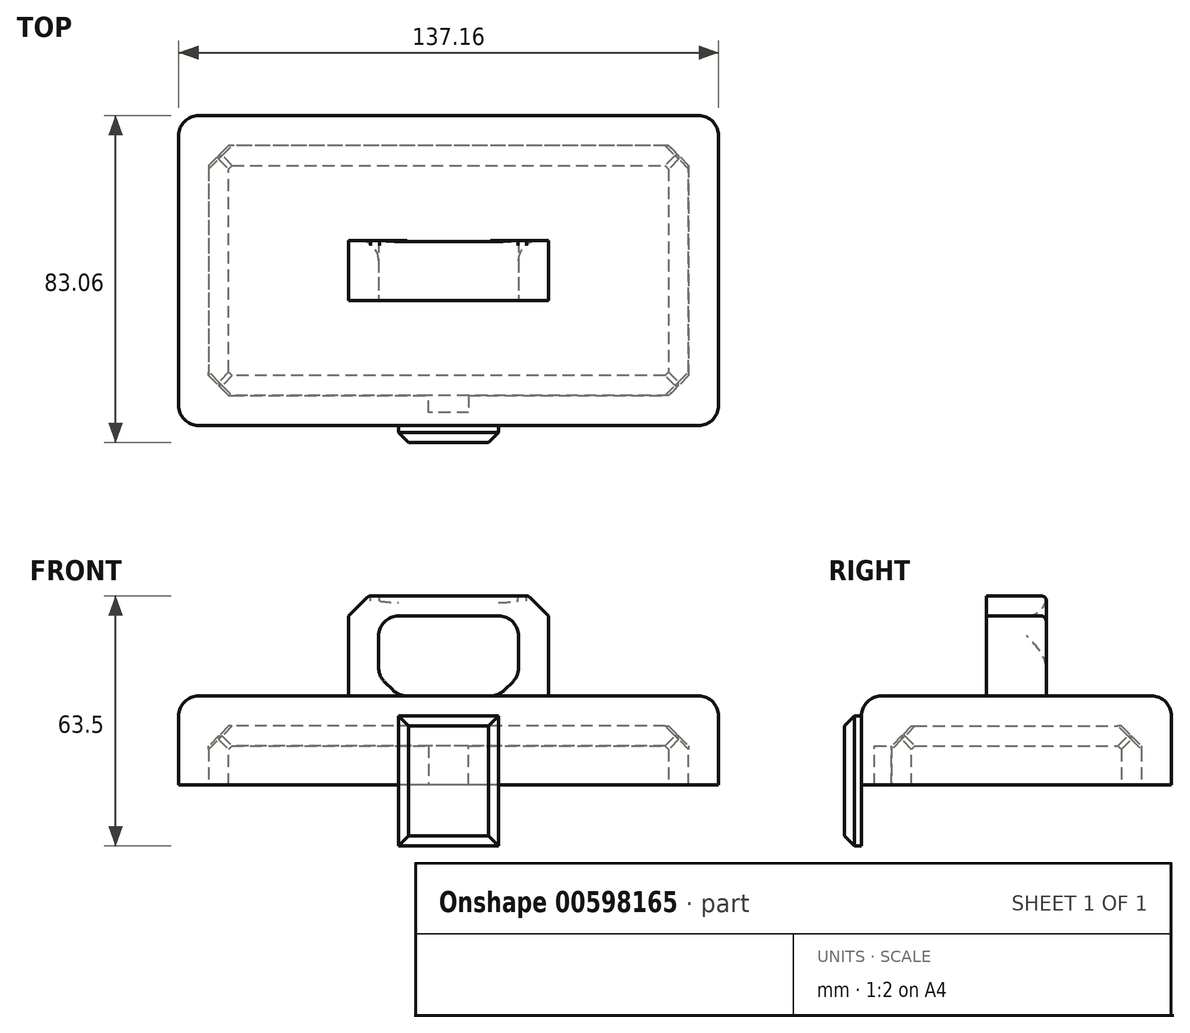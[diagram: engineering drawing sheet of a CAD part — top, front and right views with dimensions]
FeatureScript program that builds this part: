
annotation { "Feature Type Name" : "Feature", "Feature Type Description" : "" }
export const myFeature = defineFeature(function(context is Context, id is Id, definition is map)
    precondition{}
    {
        {
            var Q0;
            Q0=qCreatedBy(makeId("Top.planeOp"),FACE);
            var sketch = newSketch(context, id + "F0", { "sketchPlane" : qUnion([Q0])});
            skLineSegment(sketch, "E0.bottom", {"start": v(68.58, 39.37) * mm, "end": v(-68.58, 39.37) * mm});
            skLineSegment(sketch, "E0.top", {"start": v(68.58, -39.37) * mm, "end": v(-68.58, -39.37) * mm});
            skLineSegment(sketch, "E0.left", {"start": v(68.58, 39.37) * mm, "end": v(68.58, -39.37) * mm});
            skLineSegment(sketch, "E0.right", {"start": v(-68.58, 39.37) * mm, "end": v(-68.58, -39.37) * mm});
            skPoint(sketch, "E0.middle", {"position": v(0, 0) * mm});
            skSolve(sketch);
        }
        {
            var Q0;
            Q0 = qSketchRegion(id + "F0", true);
            extrude(context, id + "F1", {"entities" : qUnion([Q0]), "depth" : 22.6 * mm, "offsetDistance" : 25.4 * mm});
        }
        {
            var Q0;
            Q0=makeQuery(id+"F1.opExtrude","SWEPT_FACE",FACE,{"disambiguationData":[OSD([sQuery(id+"F0.wireOp",EDGE,"E0.top")])]});
            var sketch = newSketch(context, id + "F2", { "sketchPlane" : qUnion([Q0])});
            skLineSegment(sketch, "E1.bottom", {"start": v(-12.7, 17.53) * mm, "end": v(12.7, 17.53) * mm});
            skLineSegment(sketch, "E1.top", {"start": v(-12.7, -15.5) * mm, "end": v(12.7, -15.5) * mm});
            skLineSegment(sketch, "E1.left", {"start": v(-12.7, 17.53) * mm, "end": v(-12.7, -15.5) * mm});
            skLineSegment(sketch, "E1.right", {"start": v(12.7, 17.53) * mm, "end": v(12.7, -15.5) * mm});
            skSolve(sketch);
        }
        {
            var Q0;
            Q0 = qSketchRegion(id + "F2", true);
            extrude(context, id + "F3", {"entities" : qUnion([Q0]), "operationType" : NewBodyOperationType.ADD, "depth" : 4.32 * mm, "offsetDistance" : 25.4 * mm});
        }
        {
            var Q0;
            Q0=makeQuery(id+"F1.opExtrude","CAP_EDGE",EDGE,{"disambiguationData":[OSD([sQuery(id+"F0.wireOp",EDGE,"E0.right")])],"isStart":false});
            var Q1;
            Q1=makeQuery(id+"F1.opExtrude","CAP_EDGE",EDGE,{"disambiguationData":[OSD([sQuery(id+"F0.wireOp",EDGE,"E0.top")])],"isStart":false});
            var Q2;
            Q2=makeQuery(id+"F1.opExtrude","CAP_EDGE",EDGE,{"disambiguationData":[OSD([sQuery(id+"F0.wireOp",EDGE,"E0.left")])],"isStart":false});
            var Q3;
            Q3=makeQuery(id+"F1.opExtrude","CAP_EDGE",EDGE,{"disambiguationData":[OSD([sQuery(id+"F0.wireOp",EDGE,"E0.bottom")])],"isStart":false});
            var Q4;
            Q4=makeQuery(id+"F1.opExtrude","SWEPT_EDGE",EDGE,{"disambiguationData":[OSD([sQuery(id+"F0.wireOp",EDGE,"E0.top"),sQuery(id+"F0.wireOp",EDGE,"E0.left")])]});
            var Q5;
            Q5=makeQuery(id+"F1.opExtrude","SWEPT_EDGE",EDGE,{"disambiguationData":[OSD([sQuery(id+"F0.wireOp",EDGE,"E0.bottom"),sQuery(id+"F0.wireOp",EDGE,"E0.left")])]});
            var Q6;
            Q6=makeQuery(id+"F1.opExtrude","SWEPT_EDGE",EDGE,{"disambiguationData":[OSD([sQuery(id+"F0.wireOp",EDGE,"E0.top"),sQuery(id+"F0.wireOp",EDGE,"E0.right")])]});
            var Q7;
            Q7=makeQuery(id+"F1.opExtrude","SWEPT_EDGE",EDGE,{"disambiguationData":[OSD([sQuery(id+"F0.wireOp",EDGE,"E0.bottom"),sQuery(id+"F0.wireOp",EDGE,"E0.right")])]});
            fillet(context, id + "F4", {"entities" : qUnion([Q0, Q1, Q2, Q3, Q4, Q5, Q6, Q7]), "radius" : 5.08 * mm, "tangentPropagation" : true, "allowEdgeOverflow" : false});
        }
        {
            var Q0;
            Q0=makeQuery(id+"F3.opExtrude","CAP_EDGE",EDGE,{"disambiguationData":[OSD([sQuery(id+"F2.wireOp",EDGE,"E1.bottom")])],"isStart":false});
            var Q1;
            Q1=makeQuery(id+"F3.opExtrude","CAP_EDGE",EDGE,{"disambiguationData":[OSD([sQuery(id+"F2.wireOp",EDGE,"E1.right")])],"isStart":false});
            var Q2;
            Q2=makeQuery(id+"F3.opExtrude","CAP_EDGE",EDGE,{"disambiguationData":[OSD([sQuery(id+"F2.wireOp",EDGE,"E1.left")])],"isStart":false});
            var Q3;
            Q3=makeQuery(id+"F3.opExtrude","CAP_EDGE",EDGE,{"disambiguationData":[OSD([sQuery(id+"F2.wireOp",EDGE,"E1.top")])],"isStart":false});
            chamfer(context, id + "F5", {"entities" : qUnion([Q0, Q1, Q2, Q3]), "width" : 2.54 * mm, "tangentPropagation" : true});
        }
        {
            var Q0;
            Q0=makeQuery(id+"F1.opExtrude","CAP_FACE",FACE,{"disambiguationData":[OSD([sQuery(id+"F0.wireOp",EDGE,"E0.bottom"),sQuery(id+"F0.wireOp",EDGE,"E0.top"),sQuery(id+"F0.wireOp",EDGE,"E0.left"),sQuery(id+"F0.wireOp",EDGE,"E0.right")])],"isStart":true});
            shell(context, id + "F6", {"entities" : qUnion([Q0]), "thickness" : 7.62 * mm});
        }
        {
            var Q0;
            Q0=makeQuery(id+"F6.opShell","OFFSET_EDGE",EDGE,{"disambiguationData":[OSD([sQuery(id+"F0.wireOp",EDGE,"E0.bottom"),sQuery(id+"F0.wireOp",EDGE,"E0.right")])]});
            var Q1;
            Q1=makeQuery(id+"F6.opShell","OFFSET_EDGE",EDGE,{"disambiguationData":[OSD([sQuery(id+"F0.wireOp",EDGE,"E0.top"),sQuery(id+"F0.wireOp",EDGE,"E0.right")])]});
            var Q2;
            Q2=makeQuery(id+"F6.opShell","OFFSET_EDGE",EDGE,{"disambiguationData":[OSD([sQuery(id+"F0.wireOp",EDGE,"E0.bottom"),sQuery(id+"F0.wireOp",EDGE,"E0.left")])]});
            var Q3;
            Q3=makeQuery(id+"F6.opShell","OFFSET_EDGE",EDGE,{"disambiguationData":[OSD([sQuery(id+"F0.wireOp",EDGE,"E0.top"),sQuery(id+"F0.wireOp",EDGE,"E0.left")])]});
            chamfer(context, id + "F7", {"entities" : qUnion([Q0, Q1, Q2, Q3]), "width" : 5.08 * mm, "tangentPropagation" : true});
        }
        {
            var Q0;
            {var subQ0=sQuery(id+"F0.wireOp",EDGE,"E0.right");var subQ1=sQuery(id+"F0.wireOp",EDGE,"E0.left");var subQ2=sQuery(id+"F0.wireOp",EDGE,"E0.top");var subQ3=sQuery(id+"F0.wireOp",EDGE,"E0.bottom");var subQ4=makeQuery(id+"F1.opExtrude","CAP_EDGE",EDGE,{"disambiguationData":[OSD([subQ3])],"isStart":false});Q0=makeQuery(id+"F6.opShell","OFFSET_EDGE",EDGE,{"disambiguationData":[OSD([subQ3,subQ2,subQ1,subQ0]),TDD([makeQuery(id+"F4.opFillet","BLEND_EDGE",EDGE,{"blendedFrom":[subQ4,makeQuery(id+"F1.opExtrude","SWEPT_FACE",FACE,{"disambiguationData":[OSD([subQ3])]})],"blendedInto":[makeQuery(id+"F1.opExtrude","SWEPT_FACE",FACE,{"disambiguationData":[OSD([subQ3])]})]}),makeQuery(id+"F4.opFillet","BLEND_EDGE",EDGE,{"blendedFrom":[subQ4,makeQuery(id+"F1.opExtrude","CAP_FACE",FACE,{"disambiguationData":[OSD([subQ3,subQ2,subQ1,subQ0])],"isStart":false})],"blendedInto":[makeQuery(id+"F1.opExtrude","CAP_FACE",FACE,{"disambiguationData":[OSD([subQ3,subQ2,subQ1,subQ0])],"isStart":false})]})])]});}
            var Q1;
            {var subQ0=sQuery(id+"F0.wireOp",EDGE,"E0.right");var subQ1=makeQuery(id+"F1.opExtrude","CAP_EDGE",EDGE,{"disambiguationData":[OSD([subQ0])],"isStart":false});var subQ2=sQuery(id+"F0.wireOp",EDGE,"E0.left");var subQ3=sQuery(id+"F0.wireOp",EDGE,"E0.top");var subQ4=sQuery(id+"F0.wireOp",EDGE,"E0.bottom");Q1=makeQuery(id+"F6.opShell","OFFSET_EDGE",EDGE,{"disambiguationData":[OSD([subQ4,subQ3,subQ2,subQ0]),TDD([makeQuery(id+"F4.opFillet","BLEND_EDGE",EDGE,{"blendedFrom":[subQ1,makeQuery(id+"F1.opExtrude","CAP_FACE",FACE,{"disambiguationData":[OSD([subQ4,subQ3,subQ2,subQ0])],"isStart":false})],"blendedInto":[makeQuery(id+"F1.opExtrude","CAP_FACE",FACE,{"disambiguationData":[OSD([subQ4,subQ3,subQ2,subQ0])],"isStart":false})]}),makeQuery(id+"F4.opFillet","BLEND_EDGE",EDGE,{"blendedFrom":[subQ1,makeQuery(id+"F1.opExtrude","SWEPT_FACE",FACE,{"disambiguationData":[OSD([subQ0])]})],"blendedInto":[makeQuery(id+"F1.opExtrude","SWEPT_FACE",FACE,{"disambiguationData":[OSD([subQ0])]})]})])]});}
            var Q2;
            {var subQ0=sQuery(id+"F0.wireOp",EDGE,"E0.left");var subQ1=makeQuery(id+"F1.opExtrude","CAP_EDGE",EDGE,{"disambiguationData":[OSD([subQ0])],"isStart":false});var subQ2=sQuery(id+"F0.wireOp",EDGE,"E0.right");var subQ3=sQuery(id+"F0.wireOp",EDGE,"E0.top");var subQ4=sQuery(id+"F0.wireOp",EDGE,"E0.bottom");Q2=makeQuery(id+"F6.opShell","OFFSET_EDGE",EDGE,{"disambiguationData":[OSD([subQ4,subQ3,subQ0,subQ2]),TDD([makeQuery(id+"F4.opFillet","BLEND_EDGE",EDGE,{"blendedFrom":[subQ1,makeQuery(id+"F1.opExtrude","CAP_FACE",FACE,{"disambiguationData":[OSD([subQ4,subQ3,subQ0,subQ2])],"isStart":false})],"blendedInto":[makeQuery(id+"F1.opExtrude","CAP_FACE",FACE,{"disambiguationData":[OSD([subQ4,subQ3,subQ0,subQ2])],"isStart":false})]}),makeQuery(id+"F4.opFillet","BLEND_EDGE",EDGE,{"blendedFrom":[subQ1,makeQuery(id+"F1.opExtrude","SWEPT_FACE",FACE,{"disambiguationData":[OSD([subQ0])]})],"blendedInto":[makeQuery(id+"F1.opExtrude","SWEPT_FACE",FACE,{"disambiguationData":[OSD([subQ0])]})]})])]});}
            var Q3;
            {var subQ0=sQuery(id+"F0.wireOp",EDGE,"E0.top");var subQ1=makeQuery(id+"F1.opExtrude","SWEPT_FACE",FACE,{"disambiguationData":[OSD([subQ0])]});var subQ2=makeQuery(id+"F1.opExtrude","CAP_EDGE",EDGE,{"disambiguationData":[OSD([subQ0])],"isStart":false});var subQ3=sQuery(id+"F0.wireOp",EDGE,"E0.right");var subQ4=sQuery(id+"F0.wireOp",EDGE,"E0.left");var subQ5=sQuery(id+"F0.wireOp",EDGE,"E0.bottom");Q3=makeQuery(id+"F6.opShell","OFFSET_EDGE",EDGE,{"disambiguationData":[OSD([subQ5,subQ0,subQ4,subQ3]),TDD([makeQuery(id+"F4.opFillet","BLEND_EDGE",EDGE,{"blendedFrom":[subQ2,makeQuery(id+"F1.opExtrude","CAP_FACE",FACE,{"disambiguationData":[OSD([subQ5,subQ0,subQ4,subQ3])],"isStart":false})],"blendedInto":[makeQuery(id+"F1.opExtrude","CAP_FACE",FACE,{"disambiguationData":[OSD([subQ5,subQ0,subQ4,subQ3])],"isStart":false})]}),makeQuery(id+"F4.opFillet","BLEND_EDGE",EDGE,{"disambiguationData":[OD(0.0)],"blendedFrom":[subQ2,subQ1],"blendedInto":[subQ1]}),makeQuery(id+"F4.opFillet","BLEND_EDGE",EDGE,{"disambiguationData":[OD(1.0)],"blendedFrom":[subQ2,subQ1],"blendedInto":[subQ1]})])]});}
            chamfer(context, id + "F8", {"entities" : qUnion([Q0, Q1, Q2, Q3]), "width" : 5.08 * mm, "tangentPropagation" : true});
        }
        {
            var Q0;
            {var subQ0=sQuery(id+"F0.wireOp",EDGE,"E0.left");var subQ1=makeQuery(id+"F1.opExtrude","CAP_EDGE",EDGE,{"disambiguationData":[OSD([subQ0])],"isStart":false});var subQ2=sQuery(id+"F0.wireOp",EDGE,"E0.right");var subQ3=sQuery(id+"F0.wireOp",EDGE,"E0.top");var subQ4=sQuery(id+"F0.wireOp",EDGE,"E0.bottom");var subQ5=makeQuery(id+"F1.opExtrude","CAP_FACE",FACE,{"disambiguationData":[OSD([subQ4,subQ3,subQ0,subQ2])],"isStart":false});var subQ6=makeQuery(id+"F1.opExtrude","CAP_EDGE",EDGE,{"disambiguationData":[OSD([subQ4])],"isStart":false});Q0=makeQuery(id+"F8.opChamfer","BLEND_EDGE",EDGE,{"blendedFrom":[makeQuery(id+"F6.opShell","OFFSET_EDGE",EDGE,{"disambiguationData":[OSD([subQ4,subQ3,subQ0,subQ2]),TDD([makeQuery(id+"F4.opFillet","BLEND_EDGE",EDGE,{"blendedFrom":[subQ6,makeQuery(id+"F1.opExtrude","SWEPT_FACE",FACE,{"disambiguationData":[OSD([subQ4])]})],"blendedInto":[makeQuery(id+"F1.opExtrude","SWEPT_FACE",FACE,{"disambiguationData":[OSD([subQ4])]})]}),makeQuery(id+"F4.opFillet","BLEND_EDGE",EDGE,{"blendedFrom":[subQ6,subQ5],"blendedInto":[subQ5]})])]}),makeQuery(id+"F6.opShell","OFFSET_EDGE",EDGE,{"disambiguationData":[OSD([subQ4,subQ3,subQ0,subQ2]),TDD([makeQuery(id+"F4.opFillet","BLEND_EDGE",EDGE,{"blendedFrom":[subQ1,subQ5],"blendedInto":[subQ5]}),makeQuery(id+"F4.opFillet","BLEND_EDGE",EDGE,{"blendedFrom":[subQ1,makeQuery(id+"F1.opExtrude","SWEPT_FACE",FACE,{"disambiguationData":[OSD([subQ0])]})],"blendedInto":[makeQuery(id+"F1.opExtrude","SWEPT_FACE",FACE,{"disambiguationData":[OSD([subQ0])]})]})])]})],"blendedInto":[]});}
            var Q1;
            {var subQ0=sQuery(id+"F0.wireOp",EDGE,"E0.left");var subQ1=sQuery(id+"F0.wireOp",EDGE,"E0.bottom");var subQ2=sQuery(id+"F0.wireOp",EDGE,"E0.right");var subQ3=sQuery(id+"F0.wireOp",EDGE,"E0.top");var subQ4=makeQuery(id+"F1.opExtrude","CAP_EDGE",EDGE,{"disambiguationData":[OSD([subQ1])],"isStart":false});Q1=makeQuery(id+"F8.opChamfer","BLEND_EDGE",EDGE,{"blendedFrom":[makeQuery(id+"F6.opShell","OFFSET_EDGE",EDGE,{"disambiguationData":[OSD([subQ1,subQ3,subQ0,subQ2]),TDD([makeQuery(id+"F4.opFillet","BLEND_EDGE",EDGE,{"blendedFrom":[subQ4,makeQuery(id+"F1.opExtrude","SWEPT_FACE",FACE,{"disambiguationData":[OSD([subQ1])]})],"blendedInto":[makeQuery(id+"F1.opExtrude","SWEPT_FACE",FACE,{"disambiguationData":[OSD([subQ1])]})]}),makeQuery(id+"F4.opFillet","BLEND_EDGE",EDGE,{"blendedFrom":[subQ4,makeQuery(id+"F1.opExtrude","CAP_FACE",FACE,{"disambiguationData":[OSD([subQ1,subQ3,subQ0,subQ2])],"isStart":false})],"blendedInto":[makeQuery(id+"F1.opExtrude","CAP_FACE",FACE,{"disambiguationData":[OSD([subQ1,subQ3,subQ0,subQ2])],"isStart":false})]})])]}),makeQuery(id+"F7.opChamfer","BLEND_FACE",FACE,{"disambiguationData":[OSD([subQ1,subQ0])]})],"blendedInto":[makeQuery(id+"F7.opChamfer","BLEND_FACE",FACE,{"disambiguationData":[OSD([subQ1,subQ0])]})]});}
            var Q2;
            {var subQ0=sQuery(id+"F0.wireOp",EDGE,"E0.left");var subQ1=sQuery(id+"F0.wireOp",EDGE,"E0.bottom");var subQ2=makeQuery(id+"F1.opExtrude","CAP_EDGE",EDGE,{"disambiguationData":[OSD([subQ0])],"isStart":false});var subQ3=sQuery(id+"F0.wireOp",EDGE,"E0.right");var subQ4=sQuery(id+"F0.wireOp",EDGE,"E0.top");Q2=makeQuery(id+"F8.opChamfer","BLEND_EDGE",EDGE,{"blendedFrom":[makeQuery(id+"F6.opShell","OFFSET_EDGE",EDGE,{"disambiguationData":[OSD([subQ1,subQ4,subQ0,subQ3]),TDD([makeQuery(id+"F4.opFillet","BLEND_EDGE",EDGE,{"blendedFrom":[subQ2,makeQuery(id+"F1.opExtrude","CAP_FACE",FACE,{"disambiguationData":[OSD([subQ1,subQ4,subQ0,subQ3])],"isStart":false})],"blendedInto":[makeQuery(id+"F1.opExtrude","CAP_FACE",FACE,{"disambiguationData":[OSD([subQ1,subQ4,subQ0,subQ3])],"isStart":false})]}),makeQuery(id+"F4.opFillet","BLEND_EDGE",EDGE,{"blendedFrom":[subQ2,makeQuery(id+"F1.opExtrude","SWEPT_FACE",FACE,{"disambiguationData":[OSD([subQ0])]})],"blendedInto":[makeQuery(id+"F1.opExtrude","SWEPT_FACE",FACE,{"disambiguationData":[OSD([subQ0])]})]})])]}),makeQuery(id+"F7.opChamfer","BLEND_FACE",FACE,{"disambiguationData":[OSD([subQ1,subQ0])]})],"blendedInto":[makeQuery(id+"F7.opChamfer","BLEND_FACE",FACE,{"disambiguationData":[OSD([subQ1,subQ0])]})]});}
            var Q3;
            {var subQ0=sQuery(id+"F0.wireOp",EDGE,"E0.right");var subQ1=makeQuery(id+"F1.opExtrude","CAP_EDGE",EDGE,{"disambiguationData":[OSD([subQ0])],"isStart":false});var subQ2=sQuery(id+"F0.wireOp",EDGE,"E0.left");var subQ3=sQuery(id+"F0.wireOp",EDGE,"E0.top");var subQ4=sQuery(id+"F0.wireOp",EDGE,"E0.bottom");var subQ5=makeQuery(id+"F1.opExtrude","CAP_FACE",FACE,{"disambiguationData":[OSD([subQ4,subQ3,subQ2,subQ0])],"isStart":false});var subQ6=makeQuery(id+"F1.opExtrude","CAP_EDGE",EDGE,{"disambiguationData":[OSD([subQ4])],"isStart":false});Q3=makeQuery(id+"F8.opChamfer","BLEND_EDGE",EDGE,{"blendedFrom":[makeQuery(id+"F6.opShell","OFFSET_EDGE",EDGE,{"disambiguationData":[OSD([subQ4,subQ3,subQ2,subQ0]),TDD([makeQuery(id+"F4.opFillet","BLEND_EDGE",EDGE,{"blendedFrom":[subQ6,makeQuery(id+"F1.opExtrude","SWEPT_FACE",FACE,{"disambiguationData":[OSD([subQ4])]})],"blendedInto":[makeQuery(id+"F1.opExtrude","SWEPT_FACE",FACE,{"disambiguationData":[OSD([subQ4])]})]}),makeQuery(id+"F4.opFillet","BLEND_EDGE",EDGE,{"blendedFrom":[subQ6,subQ5],"blendedInto":[subQ5]})])]}),makeQuery(id+"F6.opShell","OFFSET_EDGE",EDGE,{"disambiguationData":[OSD([subQ4,subQ3,subQ2,subQ0]),TDD([makeQuery(id+"F4.opFillet","BLEND_EDGE",EDGE,{"blendedFrom":[subQ1,subQ5],"blendedInto":[subQ5]}),makeQuery(id+"F4.opFillet","BLEND_EDGE",EDGE,{"blendedFrom":[subQ1,makeQuery(id+"F1.opExtrude","SWEPT_FACE",FACE,{"disambiguationData":[OSD([subQ0])]})],"blendedInto":[makeQuery(id+"F1.opExtrude","SWEPT_FACE",FACE,{"disambiguationData":[OSD([subQ0])]})]})])]})],"blendedInto":[]});}
            var Q4;
            {var subQ0=sQuery(id+"F0.wireOp",EDGE,"E0.right");var subQ1=sQuery(id+"F0.wireOp",EDGE,"E0.bottom");var subQ2=makeQuery(id+"F1.opExtrude","CAP_EDGE",EDGE,{"disambiguationData":[OSD([subQ0])],"isStart":false});var subQ3=sQuery(id+"F0.wireOp",EDGE,"E0.left");var subQ4=sQuery(id+"F0.wireOp",EDGE,"E0.top");Q4=makeQuery(id+"F8.opChamfer","BLEND_EDGE",EDGE,{"blendedFrom":[makeQuery(id+"F6.opShell","OFFSET_EDGE",EDGE,{"disambiguationData":[OSD([subQ1,subQ4,subQ3,subQ0]),TDD([makeQuery(id+"F4.opFillet","BLEND_EDGE",EDGE,{"blendedFrom":[subQ2,makeQuery(id+"F1.opExtrude","CAP_FACE",FACE,{"disambiguationData":[OSD([subQ1,subQ4,subQ3,subQ0])],"isStart":false})],"blendedInto":[makeQuery(id+"F1.opExtrude","CAP_FACE",FACE,{"disambiguationData":[OSD([subQ1,subQ4,subQ3,subQ0])],"isStart":false})]}),makeQuery(id+"F4.opFillet","BLEND_EDGE",EDGE,{"blendedFrom":[subQ2,makeQuery(id+"F1.opExtrude","SWEPT_FACE",FACE,{"disambiguationData":[OSD([subQ0])]})],"blendedInto":[makeQuery(id+"F1.opExtrude","SWEPT_FACE",FACE,{"disambiguationData":[OSD([subQ0])]})]})])]}),makeQuery(id+"F7.opChamfer","BLEND_FACE",FACE,{"disambiguationData":[OSD([subQ1,subQ0])]})],"blendedInto":[makeQuery(id+"F7.opChamfer","BLEND_FACE",FACE,{"disambiguationData":[OSD([subQ1,subQ0])]})]});}
            var Q5;
            {var subQ0=sQuery(id+"F0.wireOp",EDGE,"E0.right");var subQ1=sQuery(id+"F0.wireOp",EDGE,"E0.bottom");var subQ2=sQuery(id+"F0.wireOp",EDGE,"E0.left");var subQ3=sQuery(id+"F0.wireOp",EDGE,"E0.top");var subQ4=makeQuery(id+"F1.opExtrude","CAP_EDGE",EDGE,{"disambiguationData":[OSD([subQ1])],"isStart":false});Q5=makeQuery(id+"F8.opChamfer","BLEND_EDGE",EDGE,{"blendedFrom":[makeQuery(id+"F6.opShell","OFFSET_EDGE",EDGE,{"disambiguationData":[OSD([subQ1,subQ3,subQ2,subQ0]),TDD([makeQuery(id+"F4.opFillet","BLEND_EDGE",EDGE,{"blendedFrom":[subQ4,makeQuery(id+"F1.opExtrude","SWEPT_FACE",FACE,{"disambiguationData":[OSD([subQ1])]})],"blendedInto":[makeQuery(id+"F1.opExtrude","SWEPT_FACE",FACE,{"disambiguationData":[OSD([subQ1])]})]}),makeQuery(id+"F4.opFillet","BLEND_EDGE",EDGE,{"blendedFrom":[subQ4,makeQuery(id+"F1.opExtrude","CAP_FACE",FACE,{"disambiguationData":[OSD([subQ1,subQ3,subQ2,subQ0])],"isStart":false})],"blendedInto":[makeQuery(id+"F1.opExtrude","CAP_FACE",FACE,{"disambiguationData":[OSD([subQ1,subQ3,subQ2,subQ0])],"isStart":false})]})])]}),makeQuery(id+"F7.opChamfer","BLEND_FACE",FACE,{"disambiguationData":[OSD([subQ1,subQ0])]})],"blendedInto":[makeQuery(id+"F7.opChamfer","BLEND_FACE",FACE,{"disambiguationData":[OSD([subQ1,subQ0])]})]});}
            var Q6;
            {var subQ0=sQuery(id+"F0.wireOp",EDGE,"E0.right");var subQ1=makeQuery(id+"F1.opExtrude","CAP_EDGE",EDGE,{"disambiguationData":[OSD([subQ0])],"isStart":false});var subQ2=sQuery(id+"F0.wireOp",EDGE,"E0.left");var subQ3=sQuery(id+"F0.wireOp",EDGE,"E0.top");var subQ4=sQuery(id+"F0.wireOp",EDGE,"E0.bottom");var subQ5=makeQuery(id+"F1.opExtrude","CAP_FACE",FACE,{"disambiguationData":[OSD([subQ4,subQ3,subQ2,subQ0])],"isStart":false});var subQ6=makeQuery(id+"F1.opExtrude","SWEPT_FACE",FACE,{"disambiguationData":[OSD([subQ3])]});var subQ7=makeQuery(id+"F1.opExtrude","CAP_EDGE",EDGE,{"disambiguationData":[OSD([subQ3])],"isStart":false});Q6=makeQuery(id+"F8.opChamfer","BLEND_EDGE",EDGE,{"blendedFrom":[makeQuery(id+"F6.opShell","OFFSET_EDGE",EDGE,{"disambiguationData":[OSD([subQ4,subQ3,subQ2,subQ0]),TDD([makeQuery(id+"F4.opFillet","BLEND_EDGE",EDGE,{"blendedFrom":[subQ7,subQ5],"blendedInto":[subQ5]}),makeQuery(id+"F4.opFillet","BLEND_EDGE",EDGE,{"disambiguationData":[OD(0.0)],"blendedFrom":[subQ7,subQ6],"blendedInto":[subQ6]}),makeQuery(id+"F4.opFillet","BLEND_EDGE",EDGE,{"disambiguationData":[OD(1.0)],"blendedFrom":[subQ7,subQ6],"blendedInto":[subQ6]})])]}),makeQuery(id+"F6.opShell","OFFSET_EDGE",EDGE,{"disambiguationData":[OSD([subQ4,subQ3,subQ2,subQ0]),TDD([makeQuery(id+"F4.opFillet","BLEND_EDGE",EDGE,{"blendedFrom":[subQ1,subQ5],"blendedInto":[subQ5]}),makeQuery(id+"F4.opFillet","BLEND_EDGE",EDGE,{"blendedFrom":[subQ1,makeQuery(id+"F1.opExtrude","SWEPT_FACE",FACE,{"disambiguationData":[OSD([subQ0])]})],"blendedInto":[makeQuery(id+"F1.opExtrude","SWEPT_FACE",FACE,{"disambiguationData":[OSD([subQ0])]})]})])]})],"blendedInto":[]});}
            var Q7;
            {var subQ0=sQuery(id+"F0.wireOp",EDGE,"E0.right");var subQ1=sQuery(id+"F0.wireOp",EDGE,"E0.top");var subQ2=makeQuery(id+"F1.opExtrude","SWEPT_FACE",FACE,{"disambiguationData":[OSD([subQ1])]});var subQ3=makeQuery(id+"F1.opExtrude","CAP_EDGE",EDGE,{"disambiguationData":[OSD([subQ1])],"isStart":false});var subQ4=sQuery(id+"F0.wireOp",EDGE,"E0.left");var subQ5=sQuery(id+"F0.wireOp",EDGE,"E0.bottom");Q7=makeQuery(id+"F8.opChamfer","BLEND_EDGE",EDGE,{"blendedFrom":[makeQuery(id+"F6.opShell","OFFSET_EDGE",EDGE,{"disambiguationData":[OSD([subQ5,subQ1,subQ4,subQ0]),TDD([makeQuery(id+"F4.opFillet","BLEND_EDGE",EDGE,{"blendedFrom":[subQ3,makeQuery(id+"F1.opExtrude","CAP_FACE",FACE,{"disambiguationData":[OSD([subQ5,subQ1,subQ4,subQ0])],"isStart":false})],"blendedInto":[makeQuery(id+"F1.opExtrude","CAP_FACE",FACE,{"disambiguationData":[OSD([subQ5,subQ1,subQ4,subQ0])],"isStart":false})]}),makeQuery(id+"F4.opFillet","BLEND_EDGE",EDGE,{"disambiguationData":[OD(0.0)],"blendedFrom":[subQ3,subQ2],"blendedInto":[subQ2]}),makeQuery(id+"F4.opFillet","BLEND_EDGE",EDGE,{"disambiguationData":[OD(1.0)],"blendedFrom":[subQ3,subQ2],"blendedInto":[subQ2]})])]}),makeQuery(id+"F7.opChamfer","BLEND_FACE",FACE,{"disambiguationData":[OSD([subQ1,subQ0])]})],"blendedInto":[makeQuery(id+"F7.opChamfer","BLEND_FACE",FACE,{"disambiguationData":[OSD([subQ1,subQ0])]})]});}
            var Q8;
            {var subQ0=sQuery(id+"F0.wireOp",EDGE,"E0.right");var subQ1=sQuery(id+"F0.wireOp",EDGE,"E0.top");var subQ2=makeQuery(id+"F1.opExtrude","CAP_EDGE",EDGE,{"disambiguationData":[OSD([subQ0])],"isStart":false});var subQ3=sQuery(id+"F0.wireOp",EDGE,"E0.left");var subQ4=sQuery(id+"F0.wireOp",EDGE,"E0.bottom");Q8=makeQuery(id+"F8.opChamfer","BLEND_EDGE",EDGE,{"blendedFrom":[makeQuery(id+"F6.opShell","OFFSET_EDGE",EDGE,{"disambiguationData":[OSD([subQ4,subQ1,subQ3,subQ0]),TDD([makeQuery(id+"F4.opFillet","BLEND_EDGE",EDGE,{"blendedFrom":[subQ2,makeQuery(id+"F1.opExtrude","CAP_FACE",FACE,{"disambiguationData":[OSD([subQ4,subQ1,subQ3,subQ0])],"isStart":false})],"blendedInto":[makeQuery(id+"F1.opExtrude","CAP_FACE",FACE,{"disambiguationData":[OSD([subQ4,subQ1,subQ3,subQ0])],"isStart":false})]}),makeQuery(id+"F4.opFillet","BLEND_EDGE",EDGE,{"blendedFrom":[subQ2,makeQuery(id+"F1.opExtrude","SWEPT_FACE",FACE,{"disambiguationData":[OSD([subQ0])]})],"blendedInto":[makeQuery(id+"F1.opExtrude","SWEPT_FACE",FACE,{"disambiguationData":[OSD([subQ0])]})]})])]}),makeQuery(id+"F7.opChamfer","BLEND_FACE",FACE,{"disambiguationData":[OSD([subQ1,subQ0])]})],"blendedInto":[makeQuery(id+"F7.opChamfer","BLEND_FACE",FACE,{"disambiguationData":[OSD([subQ1,subQ0])]})]});}
            var Q9;
            {var subQ0=sQuery(id+"F0.wireOp",EDGE,"E0.left");var subQ1=makeQuery(id+"F1.opExtrude","CAP_EDGE",EDGE,{"disambiguationData":[OSD([subQ0])],"isStart":false});var subQ2=sQuery(id+"F0.wireOp",EDGE,"E0.right");var subQ3=sQuery(id+"F0.wireOp",EDGE,"E0.top");var subQ4=sQuery(id+"F0.wireOp",EDGE,"E0.bottom");var subQ5=makeQuery(id+"F1.opExtrude","CAP_FACE",FACE,{"disambiguationData":[OSD([subQ4,subQ3,subQ0,subQ2])],"isStart":false});var subQ6=makeQuery(id+"F1.opExtrude","SWEPT_FACE",FACE,{"disambiguationData":[OSD([subQ3])]});var subQ7=makeQuery(id+"F1.opExtrude","CAP_EDGE",EDGE,{"disambiguationData":[OSD([subQ3])],"isStart":false});Q9=makeQuery(id+"F8.opChamfer","BLEND_EDGE",EDGE,{"blendedFrom":[makeQuery(id+"F6.opShell","OFFSET_EDGE",EDGE,{"disambiguationData":[OSD([subQ4,subQ3,subQ0,subQ2]),TDD([makeQuery(id+"F4.opFillet","BLEND_EDGE",EDGE,{"blendedFrom":[subQ7,subQ5],"blendedInto":[subQ5]}),makeQuery(id+"F4.opFillet","BLEND_EDGE",EDGE,{"disambiguationData":[OD(0.0)],"blendedFrom":[subQ7,subQ6],"blendedInto":[subQ6]}),makeQuery(id+"F4.opFillet","BLEND_EDGE",EDGE,{"disambiguationData":[OD(1.0)],"blendedFrom":[subQ7,subQ6],"blendedInto":[subQ6]})])]}),makeQuery(id+"F6.opShell","OFFSET_EDGE",EDGE,{"disambiguationData":[OSD([subQ4,subQ3,subQ0,subQ2]),TDD([makeQuery(id+"F4.opFillet","BLEND_EDGE",EDGE,{"blendedFrom":[subQ1,subQ5],"blendedInto":[subQ5]}),makeQuery(id+"F4.opFillet","BLEND_EDGE",EDGE,{"blendedFrom":[subQ1,makeQuery(id+"F1.opExtrude","SWEPT_FACE",FACE,{"disambiguationData":[OSD([subQ0])]})],"blendedInto":[makeQuery(id+"F1.opExtrude","SWEPT_FACE",FACE,{"disambiguationData":[OSD([subQ0])]})]})])]})],"blendedInto":[]});}
            var Q10;
            {var subQ0=sQuery(id+"F0.wireOp",EDGE,"E0.left");var subQ1=sQuery(id+"F0.wireOp",EDGE,"E0.top");var subQ2=makeQuery(id+"F1.opExtrude","CAP_EDGE",EDGE,{"disambiguationData":[OSD([subQ0])],"isStart":false});var subQ3=sQuery(id+"F0.wireOp",EDGE,"E0.right");var subQ4=sQuery(id+"F0.wireOp",EDGE,"E0.bottom");Q10=makeQuery(id+"F8.opChamfer","BLEND_EDGE",EDGE,{"blendedFrom":[makeQuery(id+"F6.opShell","OFFSET_EDGE",EDGE,{"disambiguationData":[OSD([subQ4,subQ1,subQ0,subQ3]),TDD([makeQuery(id+"F4.opFillet","BLEND_EDGE",EDGE,{"blendedFrom":[subQ2,makeQuery(id+"F1.opExtrude","CAP_FACE",FACE,{"disambiguationData":[OSD([subQ4,subQ1,subQ0,subQ3])],"isStart":false})],"blendedInto":[makeQuery(id+"F1.opExtrude","CAP_FACE",FACE,{"disambiguationData":[OSD([subQ4,subQ1,subQ0,subQ3])],"isStart":false})]}),makeQuery(id+"F4.opFillet","BLEND_EDGE",EDGE,{"blendedFrom":[subQ2,makeQuery(id+"F1.opExtrude","SWEPT_FACE",FACE,{"disambiguationData":[OSD([subQ0])]})],"blendedInto":[makeQuery(id+"F1.opExtrude","SWEPT_FACE",FACE,{"disambiguationData":[OSD([subQ0])]})]})])]}),makeQuery(id+"F7.opChamfer","BLEND_FACE",FACE,{"disambiguationData":[OSD([subQ1,subQ0])]})],"blendedInto":[makeQuery(id+"F7.opChamfer","BLEND_FACE",FACE,{"disambiguationData":[OSD([subQ1,subQ0])]})]});}
            var Q11;
            {var subQ0=sQuery(id+"F0.wireOp",EDGE,"E0.left");var subQ1=sQuery(id+"F0.wireOp",EDGE,"E0.top");var subQ2=makeQuery(id+"F1.opExtrude","SWEPT_FACE",FACE,{"disambiguationData":[OSD([subQ1])]});var subQ3=makeQuery(id+"F1.opExtrude","CAP_EDGE",EDGE,{"disambiguationData":[OSD([subQ1])],"isStart":false});var subQ4=sQuery(id+"F0.wireOp",EDGE,"E0.right");var subQ5=sQuery(id+"F0.wireOp",EDGE,"E0.bottom");Q11=makeQuery(id+"F8.opChamfer","BLEND_EDGE",EDGE,{"blendedFrom":[makeQuery(id+"F6.opShell","OFFSET_EDGE",EDGE,{"disambiguationData":[OSD([subQ5,subQ1,subQ0,subQ4]),TDD([makeQuery(id+"F4.opFillet","BLEND_EDGE",EDGE,{"blendedFrom":[subQ3,makeQuery(id+"F1.opExtrude","CAP_FACE",FACE,{"disambiguationData":[OSD([subQ5,subQ1,subQ0,subQ4])],"isStart":false})],"blendedInto":[makeQuery(id+"F1.opExtrude","CAP_FACE",FACE,{"disambiguationData":[OSD([subQ5,subQ1,subQ0,subQ4])],"isStart":false})]}),makeQuery(id+"F4.opFillet","BLEND_EDGE",EDGE,{"disambiguationData":[OD(0.0)],"blendedFrom":[subQ3,subQ2],"blendedInto":[subQ2]}),makeQuery(id+"F4.opFillet","BLEND_EDGE",EDGE,{"disambiguationData":[OD(1.0)],"blendedFrom":[subQ3,subQ2],"blendedInto":[subQ2]})])]}),makeQuery(id+"F7.opChamfer","BLEND_FACE",FACE,{"disambiguationData":[OSD([subQ1,subQ0])]})],"blendedInto":[makeQuery(id+"F7.opChamfer","BLEND_FACE",FACE,{"disambiguationData":[OSD([subQ1,subQ0])]})]});}
            chamfer(context, id + "F9", {"entities" : qUnion([Q0, Q1, Q2, Q3, Q4, Q5, Q6, Q7, Q8, Q9, Q10, Q11]), "width" : 1.27 * mm, "tangentPropagation" : true});
        }
        {
            var Q0;
            Q0=makeQuery(id+"F1.opExtrude","CAP_FACE",FACE,{"disambiguationData":[OSD([sQuery(id+"F0.wireOp",EDGE,"E0.bottom"),sQuery(id+"F0.wireOp",EDGE,"E0.top"),sQuery(id+"F0.wireOp",EDGE,"E0.left"),sQuery(id+"F0.wireOp",EDGE,"E0.right")])],"isStart":false});
            var sketch = newSketch(context, id + "F10", { "sketchPlane" : qUnion([Q0])});
            skLineSegment(sketch, "E2.bottom", {"start": v(25.4, 7.62) * mm, "end": v(-25.4, 7.62) * mm});
            skLineSegment(sketch, "E2.top", {"start": v(25.4, -7.62) * mm, "end": v(-25.4, -7.62) * mm});
            skLineSegment(sketch, "E2.left", {"start": v(25.4, 7.62) * mm, "end": v(25.4, -7.62) * mm});
            skLineSegment(sketch, "E2.right", {"start": v(-25.4, 7.62) * mm, "end": v(-25.4, -7.62) * mm});
            skPoint(sketch, "E2.middle", {"position": v(0, 0) * mm});
            skSolve(sketch);
        }
        {
            var Q0;
            Q0 = qSketchRegion(id + "F10", true);
            extrude(context, id + "F11", {"entities" : qUnion([Q0]), "operationType" : NewBodyOperationType.ADD, "depth" : 25.4 * mm, "offsetDistance" : 25.4 * mm});
        }
        {
            var Q0;
            Q0=makeQuery(id+"F11.opExtrude","SWEPT_FACE",FACE,{"disambiguationData":[OSD([sQuery(id+"F10.wireOp",EDGE,"E2.top")])]});
            var sketch = newSketch(context, id + "F12", { "sketchPlane" : qUnion([Q0])});
            skLineSegment(sketch, "E3.bottom", {"start": v(-17.78, 22.6) * mm, "end": v(17.78, 22.6) * mm});
            skLineSegment(sketch, "E3.top", {"start": v(-17.78, 42.93) * mm, "end": v(17.78, 42.93) * mm});
            skLineSegment(sketch, "E3.left", {"start": v(-17.78, 22.6) * mm, "end": v(-17.78, 42.93) * mm});
            skLineSegment(sketch, "E3.right", {"start": v(17.78, 22.6) * mm, "end": v(17.78, 42.93) * mm});
            skSolve(sketch);
        }
        {
            var Q0;
            Q0 = qSketchRegion(id + "F12", true);
            extrude(context, id + "F13", {"entities" : qUnion([Q0]), "operationType" : NewBodyOperationType.REMOVE, "oppositeDirection" : true, "depth" : 25.4 * mm, "offsetDistance" : 25.4 * mm});
        }
        {
            var Q0;
            Q0=makeQuery(id+"F11.opExtrude","CAP_EDGE",EDGE,{"disambiguationData":[OSD([sQuery(id+"F10.wireOp",EDGE,"E2.right")])],"isStart":false});
            var Q1;
            Q1=makeQuery(id+"F11.opExtrude","CAP_EDGE",EDGE,{"disambiguationData":[OSD([sQuery(id+"F10.wireOp",EDGE,"E2.left")])],"isStart":false});
            var Q2;
            Q2=makeQuery(id+"F11.opExtrude","CAP_EDGE",EDGE,{"disambiguationData":[OSD([sQuery(id+"F10.wireOp",EDGE,"E2.left")])],"isStart":true});
            var Q3;
            {var subQ0=sQuery(id+"F10.wireOp",EDGE,"E2.top");Q3=makeQuery(id+"F13.boolean.opBoolean","SPLIT",EDGE,{"disambiguationData":[TD([makeQuery(id+"F11.opExtrude","SWEPT_FACE",FACE,{"disambiguationData":[OSD([sQuery(id+"F10.wireOp",EDGE,"E2.left")])]})])],"derivedFrom":makeQuery(id+"F11.opExtrude","CAP_EDGE",EDGE,{"disambiguationData":[OSD([subQ0])],"isStart":true})});}
            var Q4;
            Q4=makeQuery(id+"F13.boolean.opBoolean","COPY",EDGE,{"derivedFrom":makeQuery(id+"F13.opExtrude","SWEPT_EDGE",EDGE,{"disambiguationData":[OSD([sQuery(id+"F10.wireOp",EDGE,"E2.top"),sQuery(id+"F12.wireOp",EDGE,"E3.bottom"),sQuery(id+"F12.wireOp",EDGE,"E3.left")])]})});
            var Q5;
            {var subQ0=sQuery(id+"F10.wireOp",EDGE,"E2.top");Q5=makeQuery(id+"F13.boolean.opBoolean","SPLIT",EDGE,{"disambiguationData":[TD([makeQuery(id+"F11.opExtrude","SWEPT_FACE",FACE,{"disambiguationData":[OSD([sQuery(id+"F10.wireOp",EDGE,"E2.right")])]})])],"derivedFrom":makeQuery(id+"F11.opExtrude","CAP_EDGE",EDGE,{"disambiguationData":[OSD([subQ0])],"isStart":true})});}
            var Q6;
            Q6=makeQuery(id+"F11.opExtrude","CAP_EDGE",EDGE,{"disambiguationData":[OSD([sQuery(id+"F10.wireOp",EDGE,"E2.right")])],"isStart":true});
            var Q7;
            {var subQ0=sQuery(id+"F10.wireOp",EDGE,"E2.bottom");Q7=makeQuery(id+"F13.boolean.opBoolean","SPLIT",EDGE,{"disambiguationData":[TD([makeQuery(id+"F11.opExtrude","SWEPT_FACE",FACE,{"disambiguationData":[OSD([sQuery(id+"F10.wireOp",EDGE,"E2.right")])]})])],"derivedFrom":makeQuery(id+"F11.opExtrude","CAP_EDGE",EDGE,{"disambiguationData":[OSD([subQ0])],"isStart":true})});}
            var Q8;
            {var subQ0=sQuery(id+"F10.wireOp",EDGE,"E2.bottom");Q8=makeQuery(id+"F13.boolean.opBoolean","SPLIT",EDGE,{"disambiguationData":[TD([makeQuery(id+"F11.opExtrude","SWEPT_FACE",FACE,{"disambiguationData":[OSD([sQuery(id+"F10.wireOp",EDGE,"E2.left")])]})])],"derivedFrom":makeQuery(id+"F11.opExtrude","CAP_EDGE",EDGE,{"disambiguationData":[OSD([subQ0])],"isStart":true})});}
            var Q9;
            Q9=makeQuery(id+"F13.boolean.opBoolean","COPY",EDGE,{"derivedFrom":makeQuery(id+"F13.opExtrude","SWEPT_EDGE",EDGE,{"disambiguationData":[OSD([sQuery(id+"F10.wireOp",EDGE,"E2.top"),sQuery(id+"F12.wireOp",EDGE,"E3.bottom"),sQuery(id+"F12.wireOp",EDGE,"E3.right")])]})});
            chamfer(context, id + "F14", {"entities" : qUnion([Q0, Q1, Q2, Q3, Q4, Q5, Q6, Q7, Q8, Q9]), "width" : 5.08 * mm, "tangentPropagation" : true});
        }
        {
            var Q0;
            {var subQ0=sQuery(id+"F10.wireOp",EDGE,"E2.left");Q0=makeQuery(id+"F14.opChamfer","BLEND_EDGE",EDGE,{"blendedFrom":[makeQuery(id+"F11.opExtrude","CAP_EDGE",EDGE,{"disambiguationData":[OSD([subQ0])],"isStart":true}),makeQuery(id+"F11.opExtrude","SWEPT_FACE",FACE,{"disambiguationData":[OSD([subQ0])]})],"blendedInto":[makeQuery(id+"F11.opExtrude","SWEPT_FACE",FACE,{"disambiguationData":[OSD([subQ0])]})]});}
            var Q1;
            {var subQ0=sQuery(id+"F10.wireOp",EDGE,"E2.top");var subQ1=makeQuery(id+"F11.opExtrude","SWEPT_FACE",FACE,{"disambiguationData":[OSD([subQ0])]});Q1=makeQuery(id+"F14.opChamfer","BLEND_EDGE",EDGE,{"blendedFrom":[makeQuery(id+"F13.boolean.opBoolean","SPLIT",EDGE,{"disambiguationData":[TD([makeQuery(id+"F11.opExtrude","SWEPT_FACE",FACE,{"disambiguationData":[OSD([sQuery(id+"F10.wireOp",EDGE,"E2.left")])]})])],"derivedFrom":makeQuery(id+"F11.opExtrude","CAP_EDGE",EDGE,{"disambiguationData":[OSD([subQ0])],"isStart":true})}),subQ1],"blendedInto":[subQ1]});}
            var Q2;
            {var subQ0=sQuery(id+"F10.wireOp",EDGE,"E2.bottom");var subQ1=makeQuery(id+"F11.opExtrude","SWEPT_FACE",FACE,{"disambiguationData":[OSD([subQ0])]});Q2=makeQuery(id+"F14.opChamfer","BLEND_EDGE",EDGE,{"blendedFrom":[makeQuery(id+"F13.boolean.opBoolean","SPLIT",EDGE,{"disambiguationData":[TD([makeQuery(id+"F11.opExtrude","SWEPT_FACE",FACE,{"disambiguationData":[OSD([sQuery(id+"F10.wireOp",EDGE,"E2.left")])]})])],"derivedFrom":makeQuery(id+"F11.opExtrude","CAP_EDGE",EDGE,{"disambiguationData":[OSD([subQ0])],"isStart":true})}),subQ1],"blendedInto":[subQ1]});}
            var Q3;
            {var subQ0=sQuery(id+"F12.wireOp",EDGE,"E3.right");Q3=makeQuery(id+"F14.opChamfer","BLEND_EDGE",EDGE,{"blendedFrom":[makeQuery(id+"F13.boolean.opBoolean","COPY",EDGE,{"derivedFrom":makeQuery(id+"F13.opExtrude","SWEPT_EDGE",EDGE,{"disambiguationData":[OSD([sQuery(id+"F10.wireOp",EDGE,"E2.top"),sQuery(id+"F12.wireOp",EDGE,"E3.bottom"),subQ0])]})}),makeQuery(id+"F13.boolean.opBoolean","COPY",FACE,{"derivedFrom":makeQuery(id+"F13.opExtrude","SWEPT_FACE",FACE,{"disambiguationData":[OSD([subQ0])]})})],"blendedInto":[makeQuery(id+"F13.boolean.opBoolean","COPY",FACE,{"derivedFrom":makeQuery(id+"F13.opExtrude","SWEPT_FACE",FACE,{"disambiguationData":[OSD([subQ0])]})})]});}
            var Q4;
            {var subQ0=sQuery(id+"F10.wireOp",EDGE,"E2.bottom");var subQ1=makeQuery(id+"F11.opExtrude","SWEPT_FACE",FACE,{"disambiguationData":[OSD([subQ0])]});Q4=makeQuery(id+"F14.opChamfer","BLEND_EDGE",EDGE,{"blendedFrom":[makeQuery(id+"F13.boolean.opBoolean","SPLIT",EDGE,{"disambiguationData":[TD([makeQuery(id+"F11.opExtrude","SWEPT_FACE",FACE,{"disambiguationData":[OSD([sQuery(id+"F10.wireOp",EDGE,"E2.right")])]})])],"derivedFrom":makeQuery(id+"F11.opExtrude","CAP_EDGE",EDGE,{"disambiguationData":[OSD([subQ0])],"isStart":true})}),subQ1],"blendedInto":[subQ1]});}
            var Q5;
            {var subQ0=sQuery(id+"F10.wireOp",EDGE,"E2.right");Q5=makeQuery(id+"F14.opChamfer","BLEND_EDGE",EDGE,{"blendedFrom":[makeQuery(id+"F11.opExtrude","CAP_EDGE",EDGE,{"disambiguationData":[OSD([subQ0])],"isStart":true}),makeQuery(id+"F11.opExtrude","SWEPT_FACE",FACE,{"disambiguationData":[OSD([subQ0])]})],"blendedInto":[makeQuery(id+"F11.opExtrude","SWEPT_FACE",FACE,{"disambiguationData":[OSD([subQ0])]})]});}
            var Q6;
            {var subQ0=sQuery(id+"F10.wireOp",EDGE,"E2.top");var subQ1=makeQuery(id+"F11.opExtrude","SWEPT_FACE",FACE,{"disambiguationData":[OSD([subQ0])]});Q6=makeQuery(id+"F14.opChamfer","BLEND_EDGE",EDGE,{"blendedFrom":[makeQuery(id+"F13.boolean.opBoolean","SPLIT",EDGE,{"disambiguationData":[TD([makeQuery(id+"F11.opExtrude","SWEPT_FACE",FACE,{"disambiguationData":[OSD([sQuery(id+"F10.wireOp",EDGE,"E2.right")])]})])],"derivedFrom":makeQuery(id+"F11.opExtrude","CAP_EDGE",EDGE,{"disambiguationData":[OSD([subQ0])],"isStart":true})}),subQ1],"blendedInto":[subQ1]});}
            var Q7;
            {var subQ0=sQuery(id+"F12.wireOp",EDGE,"E3.left");Q7=makeQuery(id+"F14.opChamfer","BLEND_EDGE",EDGE,{"blendedFrom":[makeQuery(id+"F13.boolean.opBoolean","COPY",EDGE,{"derivedFrom":makeQuery(id+"F13.opExtrude","SWEPT_EDGE",EDGE,{"disambiguationData":[OSD([sQuery(id+"F10.wireOp",EDGE,"E2.top"),sQuery(id+"F12.wireOp",EDGE,"E3.bottom"),subQ0])]})}),makeQuery(id+"F13.boolean.opBoolean","COPY",FACE,{"derivedFrom":makeQuery(id+"F13.opExtrude","SWEPT_FACE",FACE,{"disambiguationData":[OSD([subQ0])]})})],"blendedInto":[makeQuery(id+"F13.boolean.opBoolean","COPY",FACE,{"derivedFrom":makeQuery(id+"F13.opExtrude","SWEPT_FACE",FACE,{"disambiguationData":[OSD([subQ0])]})})]});}
            fillet(context, id + "F15", {"entities" : qUnion([Q0, Q1, Q2, Q3, Q4, Q5, Q6, Q7]), "radius" : 5.08 * mm, "tangentPropagation" : true, "allowEdgeOverflow" : false});
        }
        {
            var Q0;
            Q0=makeQuery(id+"F14.opChamfer","BLEND_EDGE",EDGE,{"blendedFrom":[makeQuery(id+"F11.opExtrude","CAP_EDGE",EDGE,{"disambiguationData":[OSD([sQuery(id+"F10.wireOp",EDGE,"E2.left")])],"isStart":true}),makeQuery(id+"F13.boolean.opBoolean","MERGE",FACE,{"derivedFrom":[makeQuery(id+"F1.opExtrude","CAP_FACE",FACE,{"disambiguationData":[OSD([sQuery(id+"F0.wireOp",EDGE,"E0.bottom"),sQuery(id+"F0.wireOp",EDGE,"E0.top"),sQuery(id+"F0.wireOp",EDGE,"E0.left"),sQuery(id+"F0.wireOp",EDGE,"E0.right")])],"isStart":false}),makeQuery(id+"F13.opExtrude","SWEPT_FACE",FACE,{"disambiguationData":[OSD([sQuery(id+"F12.wireOp",EDGE,"E3.bottom")])]})]})],"blendedInto":[makeQuery(id+"F13.boolean.opBoolean","MERGE",FACE,{"derivedFrom":[makeQuery(id+"F1.opExtrude","CAP_FACE",FACE,{"disambiguationData":[OSD([sQuery(id+"F0.wireOp",EDGE,"E0.bottom"),sQuery(id+"F0.wireOp",EDGE,"E0.top"),sQuery(id+"F0.wireOp",EDGE,"E0.left"),sQuery(id+"F0.wireOp",EDGE,"E0.right")])],"isStart":false}),makeQuery(id+"F13.opExtrude","SWEPT_FACE",FACE,{"disambiguationData":[OSD([sQuery(id+"F12.wireOp",EDGE,"E3.bottom")])]})]})]});
            var Q1;
            {var subQ0=makeQuery(id+"F13.opExtrude","SWEPT_FACE",FACE,{"disambiguationData":[OSD([sQuery(id+"F12.wireOp",EDGE,"E3.bottom")])]});var subQ1=makeQuery(id+"F1.opExtrude","CAP_FACE",FACE,{"disambiguationData":[OSD([sQuery(id+"F0.wireOp",EDGE,"E0.bottom"),sQuery(id+"F0.wireOp",EDGE,"E0.top"),sQuery(id+"F0.wireOp",EDGE,"E0.left"),sQuery(id+"F0.wireOp",EDGE,"E0.right")])],"isStart":false});var subQ2=sQuery(id+"F10.wireOp",EDGE,"E2.top");Q1=makeQuery(id+"F14.opChamfer","BLEND_EDGE",EDGE,{"blendedFrom":[makeQuery(id+"F13.boolean.opBoolean","SPLIT",EDGE,{"disambiguationData":[TD([makeQuery(id+"F11.opExtrude","SWEPT_FACE",FACE,{"disambiguationData":[OSD([sQuery(id+"F10.wireOp",EDGE,"E2.left")])]})])],"derivedFrom":makeQuery(id+"F11.opExtrude","CAP_EDGE",EDGE,{"disambiguationData":[OSD([subQ2])],"isStart":true})}),makeQuery(id+"F13.boolean.opBoolean","MERGE",FACE,{"derivedFrom":[subQ1,subQ0]})],"blendedInto":[makeQuery(id+"F13.boolean.opBoolean","MERGE",FACE,{"derivedFrom":[subQ1,subQ0]})]});}
            var Q2;
            {var subQ0=makeQuery(id+"F13.opExtrude","SWEPT_FACE",FACE,{"disambiguationData":[OSD([sQuery(id+"F12.wireOp",EDGE,"E3.bottom")])]});var subQ1=makeQuery(id+"F1.opExtrude","CAP_FACE",FACE,{"disambiguationData":[OSD([sQuery(id+"F0.wireOp",EDGE,"E0.bottom"),sQuery(id+"F0.wireOp",EDGE,"E0.top"),sQuery(id+"F0.wireOp",EDGE,"E0.left"),sQuery(id+"F0.wireOp",EDGE,"E0.right")])],"isStart":false});var subQ2=sQuery(id+"F10.wireOp",EDGE,"E2.bottom");Q2=makeQuery(id+"F14.opChamfer","BLEND_EDGE",EDGE,{"blendedFrom":[makeQuery(id+"F13.boolean.opBoolean","SPLIT",EDGE,{"disambiguationData":[TD([makeQuery(id+"F11.opExtrude","SWEPT_FACE",FACE,{"disambiguationData":[OSD([sQuery(id+"F10.wireOp",EDGE,"E2.left")])]})])],"derivedFrom":makeQuery(id+"F11.opExtrude","CAP_EDGE",EDGE,{"disambiguationData":[OSD([subQ2])],"isStart":true})}),makeQuery(id+"F13.boolean.opBoolean","MERGE",FACE,{"derivedFrom":[subQ1,subQ0]})],"blendedInto":[makeQuery(id+"F13.boolean.opBoolean","MERGE",FACE,{"derivedFrom":[subQ1,subQ0]})]});}
            var Q3;
            {var subQ0=sQuery(id+"F12.wireOp",EDGE,"E3.bottom");Q3=makeQuery(id+"F14.opChamfer","BLEND_EDGE",EDGE,{"blendedFrom":[makeQuery(id+"F13.boolean.opBoolean","COPY",EDGE,{"derivedFrom":makeQuery(id+"F13.opExtrude","SWEPT_EDGE",EDGE,{"disambiguationData":[OSD([sQuery(id+"F10.wireOp",EDGE,"E2.top"),subQ0,sQuery(id+"F12.wireOp",EDGE,"E3.right")])]})}),makeQuery(id+"F13.boolean.opBoolean","MERGE",FACE,{"derivedFrom":[makeQuery(id+"F1.opExtrude","CAP_FACE",FACE,{"disambiguationData":[OSD([sQuery(id+"F0.wireOp",EDGE,"E0.bottom"),sQuery(id+"F0.wireOp",EDGE,"E0.top"),sQuery(id+"F0.wireOp",EDGE,"E0.left"),sQuery(id+"F0.wireOp",EDGE,"E0.right")])],"isStart":false}),makeQuery(id+"F13.opExtrude","SWEPT_FACE",FACE,{"disambiguationData":[OSD([subQ0])]})]})],"blendedInto":[makeQuery(id+"F13.boolean.opBoolean","MERGE",FACE,{"derivedFrom":[makeQuery(id+"F1.opExtrude","CAP_FACE",FACE,{"disambiguationData":[OSD([sQuery(id+"F0.wireOp",EDGE,"E0.bottom"),sQuery(id+"F0.wireOp",EDGE,"E0.top"),sQuery(id+"F0.wireOp",EDGE,"E0.left"),sQuery(id+"F0.wireOp",EDGE,"E0.right")])],"isStart":false}),makeQuery(id+"F13.opExtrude","SWEPT_FACE",FACE,{"disambiguationData":[OSD([subQ0])]})]})]});}
            fillet(context, id + "F16", {"entities" : qUnion([Q0, Q1, Q2, Q3]), "radius" : 5.08 * mm, "tangentPropagation" : true, "allowEdgeOverflow" : false});
        }
        {
            var Q0;
            {var subQ0=sQuery(id+"F12.wireOp",EDGE,"E3.bottom");Q0=makeQuery(id+"F14.opChamfer","BLEND_EDGE",EDGE,{"blendedFrom":[makeQuery(id+"F13.boolean.opBoolean","COPY",EDGE,{"derivedFrom":makeQuery(id+"F13.opExtrude","SWEPT_EDGE",EDGE,{"disambiguationData":[OSD([sQuery(id+"F10.wireOp",EDGE,"E2.top"),subQ0,sQuery(id+"F12.wireOp",EDGE,"E3.left")])]})}),makeQuery(id+"F13.boolean.opBoolean","MERGE",FACE,{"derivedFrom":[makeQuery(id+"F1.opExtrude","CAP_FACE",FACE,{"disambiguationData":[OSD([sQuery(id+"F0.wireOp",EDGE,"E0.bottom"),sQuery(id+"F0.wireOp",EDGE,"E0.top"),sQuery(id+"F0.wireOp",EDGE,"E0.left"),sQuery(id+"F0.wireOp",EDGE,"E0.right")])],"isStart":false}),makeQuery(id+"F13.opExtrude","SWEPT_FACE",FACE,{"disambiguationData":[OSD([subQ0])]})]})],"blendedInto":[makeQuery(id+"F13.boolean.opBoolean","MERGE",FACE,{"derivedFrom":[makeQuery(id+"F1.opExtrude","CAP_FACE",FACE,{"disambiguationData":[OSD([sQuery(id+"F0.wireOp",EDGE,"E0.bottom"),sQuery(id+"F0.wireOp",EDGE,"E0.top"),sQuery(id+"F0.wireOp",EDGE,"E0.left"),sQuery(id+"F0.wireOp",EDGE,"E0.right")])],"isStart":false}),makeQuery(id+"F13.opExtrude","SWEPT_FACE",FACE,{"disambiguationData":[OSD([subQ0])]})]})]});}
            var Q1;
            {var subQ0=makeQuery(id+"F13.opExtrude","SWEPT_FACE",FACE,{"disambiguationData":[OSD([sQuery(id+"F12.wireOp",EDGE,"E3.bottom")])]});var subQ1=makeQuery(id+"F1.opExtrude","CAP_FACE",FACE,{"disambiguationData":[OSD([sQuery(id+"F0.wireOp",EDGE,"E0.bottom"),sQuery(id+"F0.wireOp",EDGE,"E0.top"),sQuery(id+"F0.wireOp",EDGE,"E0.left"),sQuery(id+"F0.wireOp",EDGE,"E0.right")])],"isStart":false});var subQ2=sQuery(id+"F10.wireOp",EDGE,"E2.top");Q1=makeQuery(id+"F14.opChamfer","BLEND_EDGE",EDGE,{"blendedFrom":[makeQuery(id+"F13.boolean.opBoolean","SPLIT",EDGE,{"disambiguationData":[TD([makeQuery(id+"F11.opExtrude","SWEPT_FACE",FACE,{"disambiguationData":[OSD([sQuery(id+"F10.wireOp",EDGE,"E2.right")])]})])],"derivedFrom":makeQuery(id+"F11.opExtrude","CAP_EDGE",EDGE,{"disambiguationData":[OSD([subQ2])],"isStart":true})}),makeQuery(id+"F13.boolean.opBoolean","MERGE",FACE,{"derivedFrom":[subQ1,subQ0]})],"blendedInto":[makeQuery(id+"F13.boolean.opBoolean","MERGE",FACE,{"derivedFrom":[subQ1,subQ0]})]});}
            var Q2;
            Q2=makeQuery(id+"F14.opChamfer","BLEND_EDGE",EDGE,{"blendedFrom":[makeQuery(id+"F11.opExtrude","CAP_EDGE",EDGE,{"disambiguationData":[OSD([sQuery(id+"F10.wireOp",EDGE,"E2.right")])],"isStart":true}),makeQuery(id+"F13.boolean.opBoolean","MERGE",FACE,{"derivedFrom":[makeQuery(id+"F1.opExtrude","CAP_FACE",FACE,{"disambiguationData":[OSD([sQuery(id+"F0.wireOp",EDGE,"E0.bottom"),sQuery(id+"F0.wireOp",EDGE,"E0.top"),sQuery(id+"F0.wireOp",EDGE,"E0.left"),sQuery(id+"F0.wireOp",EDGE,"E0.right")])],"isStart":false}),makeQuery(id+"F13.opExtrude","SWEPT_FACE",FACE,{"disambiguationData":[OSD([sQuery(id+"F12.wireOp",EDGE,"E3.bottom")])]})]})],"blendedInto":[makeQuery(id+"F13.boolean.opBoolean","MERGE",FACE,{"derivedFrom":[makeQuery(id+"F1.opExtrude","CAP_FACE",FACE,{"disambiguationData":[OSD([sQuery(id+"F0.wireOp",EDGE,"E0.bottom"),sQuery(id+"F0.wireOp",EDGE,"E0.top"),sQuery(id+"F0.wireOp",EDGE,"E0.left"),sQuery(id+"F0.wireOp",EDGE,"E0.right")])],"isStart":false}),makeQuery(id+"F13.opExtrude","SWEPT_FACE",FACE,{"disambiguationData":[OSD([sQuery(id+"F12.wireOp",EDGE,"E3.bottom")])]})]})]});
            var Q3;
            {var subQ0=makeQuery(id+"F13.opExtrude","SWEPT_FACE",FACE,{"disambiguationData":[OSD([sQuery(id+"F12.wireOp",EDGE,"E3.bottom")])]});var subQ1=makeQuery(id+"F1.opExtrude","CAP_FACE",FACE,{"disambiguationData":[OSD([sQuery(id+"F0.wireOp",EDGE,"E0.bottom"),sQuery(id+"F0.wireOp",EDGE,"E0.top"),sQuery(id+"F0.wireOp",EDGE,"E0.left"),sQuery(id+"F0.wireOp",EDGE,"E0.right")])],"isStart":false});var subQ2=sQuery(id+"F10.wireOp",EDGE,"E2.bottom");Q3=makeQuery(id+"F14.opChamfer","BLEND_EDGE",EDGE,{"blendedFrom":[makeQuery(id+"F13.boolean.opBoolean","SPLIT",EDGE,{"disambiguationData":[TD([makeQuery(id+"F11.opExtrude","SWEPT_FACE",FACE,{"disambiguationData":[OSD([sQuery(id+"F10.wireOp",EDGE,"E2.right")])]})])],"derivedFrom":makeQuery(id+"F11.opExtrude","CAP_EDGE",EDGE,{"disambiguationData":[OSD([subQ2])],"isStart":true})}),makeQuery(id+"F13.boolean.opBoolean","MERGE",FACE,{"derivedFrom":[subQ1,subQ0]})],"blendedInto":[makeQuery(id+"F13.boolean.opBoolean","MERGE",FACE,{"derivedFrom":[subQ1,subQ0]})]});}
            fillet(context, id + "F17", {"entities" : qUnion([Q0, Q1, Q2, Q3]), "radius" : 5.08 * mm, "tangentPropagation" : true, "allowEdgeOverflow" : false});
        }
        {
            var Q0;
            Q0=makeQuery(id+"F13.boolean.opBoolean","COPY",EDGE,{"derivedFrom":makeQuery(id+"F13.opExtrude","SWEPT_EDGE",EDGE,{"disambiguationData":[OSD([sQuery(id+"F12.wireOp",EDGE,"E3.top"),sQuery(id+"F12.wireOp",EDGE,"E3.right")])]})});
            var Q1;
            Q1=makeQuery(id+"F13.boolean.opBoolean","COPY",EDGE,{"derivedFrom":makeQuery(id+"F13.opExtrude","SWEPT_EDGE",EDGE,{"disambiguationData":[OSD([sQuery(id+"F12.wireOp",EDGE,"E3.top"),sQuery(id+"F12.wireOp",EDGE,"E3.left")])]})});
            var Q2;
            Q2=makeQuery(id+"F13.boolean.opBoolean","COPY",EDGE,{"derivedFrom":makeQuery(id+"F13.opExtrude","CAP_EDGE",EDGE,{"disambiguationData":[OSD([sQuery(id+"F12.wireOp",EDGE,"E3.top")])],"isStart":true})});
            var Q3;
            Q3=makeQuery(id+"F13.boolean.opBoolean","INTERSECT",EDGE,{"derivedFrom":[makeQuery(id+"F11.opExtrude","SWEPT_FACE",FACE,{"disambiguationData":[OSD([sQuery(id+"F10.wireOp",EDGE,"E2.bottom")])]}),makeQuery(id+"F13.opExtrude","SWEPT_FACE",FACE,{"disambiguationData":[OSD([sQuery(id+"F12.wireOp",EDGE,"E3.top")])]})]});
            fillet(context, id + "F18", {"entities" : qUnion([Q0, Q1, Q2, Q3]), "radius" : 5.08 * mm, "tangentPropagation" : true, "allowEdgeOverflow" : false});
        }
        {
            var Q0;
            {var subQ0=sQuery(id+"F10.wireOp",EDGE,"E2.bottom");Q0=makeQuery(id+"F18.opFillet","BLEND_EDGE",EDGE,{"blendedFrom":[makeQuery(id+"F13.boolean.opBoolean","INTERSECT",EDGE,{"derivedFrom":[makeQuery(id+"F11.opExtrude","SWEPT_FACE",FACE,{"disambiguationData":[OSD([subQ0])]}),makeQuery(id+"F13.opExtrude","SWEPT_FACE",FACE,{"disambiguationData":[OSD([sQuery(id+"F12.wireOp",EDGE,"E3.top")])]})]}),makeQuery(id+"F11.opExtrude","CAP_FACE",FACE,{"disambiguationData":[OSD([subQ0,sQuery(id+"F10.wireOp",EDGE,"E2.top"),sQuery(id+"F10.wireOp",EDGE,"E2.left"),sQuery(id+"F10.wireOp",EDGE,"E2.right")])],"isStart":false})],"blendedInto":[makeQuery(id+"F11.opExtrude","CAP_FACE",FACE,{"disambiguationData":[OSD([subQ0,sQuery(id+"F10.wireOp",EDGE,"E2.top"),sQuery(id+"F10.wireOp",EDGE,"E2.left"),sQuery(id+"F10.wireOp",EDGE,"E2.right")])],"isStart":false})]});}
            var Q1;
            Q1=makeQuery(id+"F18.opFillet","BLEND_EDGE",EDGE,{"blendedFrom":[makeQuery(id+"F13.boolean.opBoolean","COPY",EDGE,{"derivedFrom":makeQuery(id+"F13.opExtrude","CAP_EDGE",EDGE,{"disambiguationData":[OSD([sQuery(id+"F12.wireOp",EDGE,"E3.top")])],"isStart":true})}),makeQuery(id+"F11.opExtrude","CAP_FACE",FACE,{"disambiguationData":[OSD([sQuery(id+"F10.wireOp",EDGE,"E2.bottom"),sQuery(id+"F10.wireOp",EDGE,"E2.top"),sQuery(id+"F10.wireOp",EDGE,"E2.left"),sQuery(id+"F10.wireOp",EDGE,"E2.right")])],"isStart":false})],"blendedInto":[makeQuery(id+"F11.opExtrude","CAP_FACE",FACE,{"disambiguationData":[OSD([sQuery(id+"F10.wireOp",EDGE,"E2.bottom"),sQuery(id+"F10.wireOp",EDGE,"E2.top"),sQuery(id+"F10.wireOp",EDGE,"E2.left"),sQuery(id+"F10.wireOp",EDGE,"E2.right")])],"isStart":false})]});
            fillet(context, id + "F19", {"entities" : qUnion([Q0, Q1]), "radius" : 1.27 * mm, "tangentPropagation" : true, "allowEdgeOverflow" : false});
        }
        {
            var Q0;
            {var subQ0=sQuery(id+"F10.wireOp",EDGE,"E2.left");Q0=makeQuery(id+"F14.opChamfer","BLEND_EDGE",EDGE,{"blendedFrom":[makeQuery(id+"F11.opExtrude","CAP_EDGE",EDGE,{"disambiguationData":[OSD([subQ0])],"isStart":false}),makeQuery(id+"F11.opExtrude","CAP_FACE",FACE,{"disambiguationData":[OSD([sQuery(id+"F10.wireOp",EDGE,"E2.bottom"),sQuery(id+"F10.wireOp",EDGE,"E2.top"),subQ0,sQuery(id+"F10.wireOp",EDGE,"E2.right")])],"isStart":false})],"blendedInto":[makeQuery(id+"F11.opExtrude","CAP_FACE",FACE,{"disambiguationData":[OSD([sQuery(id+"F10.wireOp",EDGE,"E2.bottom"),sQuery(id+"F10.wireOp",EDGE,"E2.top"),subQ0,sQuery(id+"F10.wireOp",EDGE,"E2.right")])],"isStart":false})]});}
            var Q1;
            {var subQ0=sQuery(id+"F10.wireOp",EDGE,"E2.right");Q1=makeQuery(id+"F14.opChamfer","BLEND_EDGE",EDGE,{"blendedFrom":[makeQuery(id+"F11.opExtrude","CAP_EDGE",EDGE,{"disambiguationData":[OSD([subQ0])],"isStart":false}),makeQuery(id+"F11.opExtrude","CAP_FACE",FACE,{"disambiguationData":[OSD([sQuery(id+"F10.wireOp",EDGE,"E2.bottom"),sQuery(id+"F10.wireOp",EDGE,"E2.top"),sQuery(id+"F10.wireOp",EDGE,"E2.left"),subQ0])],"isStart":false})],"blendedInto":[makeQuery(id+"F11.opExtrude","CAP_FACE",FACE,{"disambiguationData":[OSD([sQuery(id+"F10.wireOp",EDGE,"E2.bottom"),sQuery(id+"F10.wireOp",EDGE,"E2.top"),sQuery(id+"F10.wireOp",EDGE,"E2.left"),subQ0])],"isStart":false})]});}
            fillet(context, id + "F20", {"entities" : qUnion([Q0, Q1]), "radius" : 1.27 * mm, "tangentPropagation" : true, "allowEdgeOverflow" : false});
        }
    });
